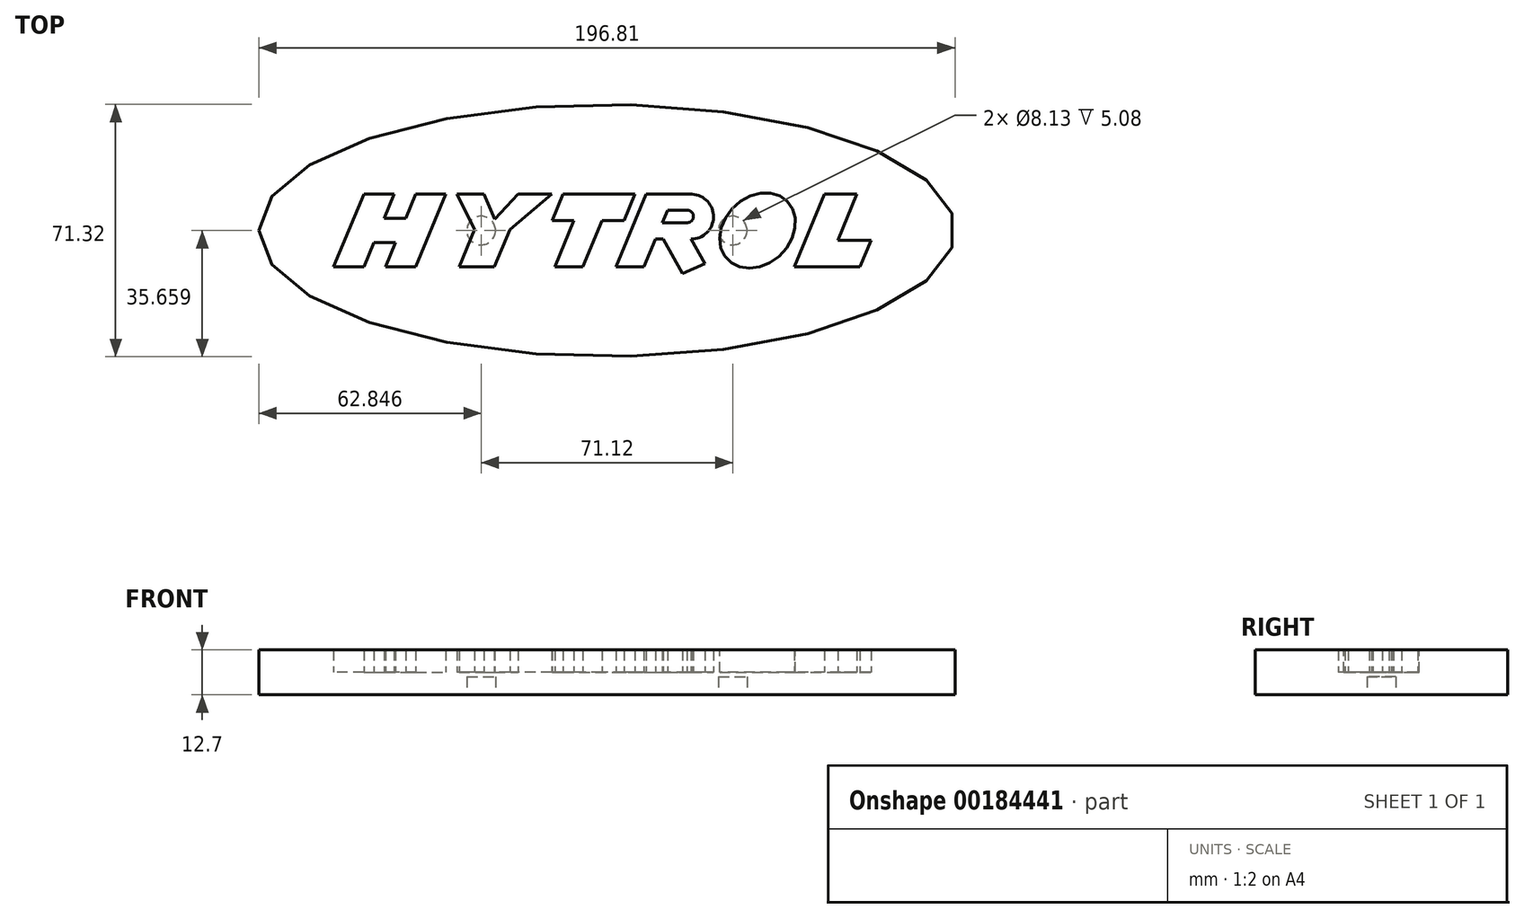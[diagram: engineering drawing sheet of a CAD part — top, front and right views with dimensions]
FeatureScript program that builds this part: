
annotation { "Feature Type Name" : "Feature", "Feature Type Description" : "" }
export const myFeature = defineFeature(function(context is Context, id is Id, definition is map)
    precondition{}
    {
        {
            var Q0;
            Q0=qCreatedBy(makeId("Top.planeOp"),FACE);
            var sketch = newSketch(context, id + "F0", { "sketchPlane" : qUnion([Q0])});
            skLineSegment(sketch, "E0", {"start": v(-38.3, -9.11) * mm, "end": v(-29.76, -9.11) * mm});
            skLineSegment(sketch, "E1", {"start": v(-29.76, 11.4) * mm, "end": v(-38.3, -9.11) * mm});
            skLineSegment(sketch, "E2", {"start": v(-29.76, 11.4) * mm, "end": v(-21.22, 11.4) * mm});
            skLineSegment(sketch, "E3", {"start": v(-6.55, 11.4) * mm, "end": v(-15.1, -9.11) * mm});
            skLineSegment(sketch, "E4", {"start": v(-15.1, -9.11) * mm, "end": v(-23.63, -9.11) * mm});
            skLineSegment(sketch, "E5", {"start": v(-23.63, -9.11) * mm, "end": v(-20.79, -2.28) * mm});
            skLineSegment(sketch, "E6", {"start": v(-29.76, -9.11) * mm, "end": v(-26.92, -2.28) * mm});
            skLineSegment(sketch, "E7", {"start": v(-26.92, -2.28) * mm, "end": v(-20.79, -2.28) * mm});
            skLineSegment(sketch, "E8", {"start": v(-21.22, 11.4) * mm, "end": v(-24.06, 4.58) * mm});
            skLineSegment(sketch, "E9", {"start": v(-24.06, 4.58) * mm, "end": v(-17.93, 4.58) * mm});
            skLineSegment(sketch, "E10.trimOffspring", {"start": v(-24.06, 4.58) * mm, "end": v(-21.22, 11.4) * mm});
            skLineSegment(sketch, "E11.trimOffspring", {"start": v(-17.93, 4.58) * mm, "end": v(-15.1, 11.4) * mm});
            skLineSegment(sketch, "E12.trimOffspring", {"start": v(-15.1, 11.4) * mm, "end": v(-6.55, 11.4) * mm});
            skLineSegment(sketch, "E13", {"start": v(-6.55, 11.4) * mm, "end": v(-3.38, 11.4) * mm, "construction": true});
            skLineSegment(sketch, "E14", {"start": v(-15.1, -9.11) * mm, "end": v(-2.83, -9.11) * mm, "construction": true});
            skLineSegment(sketch, "E15", {"start": v(-2.83, -9.11) * mm, "end": v(1.56, 1.44) * mm});
            skLineSegment(sketch, "E16", {"start": v(1.56, 1.44) * mm, "end": v(-3.38, 11.4) * mm});
            skLineSegment(sketch, "E17", {"start": v(-2.83, -9.11) * mm, "end": v(7.13, -9.11) * mm});
            skLineSegment(sketch, "E18", {"start": v(23.36, 11.4) * mm, "end": v(13.84, 11.4) * mm});
            skLineSegment(sketch, "E19", {"start": v(4.24, 11.4) * mm, "end": v(-3.38, 11.4) * mm});
            skLineSegment(sketch, "E20", {"start": v(23.36, 11.4) * mm, "end": v(11.52, 1.44) * mm});
            skLineSegment(sketch, "E21", {"start": v(11.52, 1.44) * mm, "end": v(7.13, -9.11) * mm});
            skLineSegment(sketch, "E22", {"start": v(7.17, 4.38) * mm, "end": v(13.84, 11.4) * mm});
            skLineSegment(sketch, "E23", {"start": v(2.15, -9.11) * mm, "end": v(7.17, 4.38) * mm, "construction": true});
            skLineSegment(sketch, "E24", {"start": v(4.24, 11.4) * mm, "end": v(7.17, 4.38) * mm});
            skLineSegment(sketch, "E25", {"start": v(7.13, -9.11) * mm, "end": v(24.2, -9.11) * mm, "construction": true});
            skLineSegment(sketch, "E26", {"start": v(23.36, 11.4) * mm, "end": v(26.54, 11.4) * mm, "construction": true});
            skLineSegment(sketch, "E27", {"start": v(4.24, 11.4) * mm, "end": v(13.84, 11.4) * mm, "construction": true});
            skLineSegment(sketch, "E28", {"start": v(26.54, 11.4) * mm, "end": v(23.46, 4) * mm});
            skLineSegment(sketch, "E29", {"start": v(23.46, 4) * mm, "end": v(29.66, 4) * mm});
            skLineSegment(sketch, "E30", {"start": v(29.66, 4) * mm, "end": v(24.2, -9.11) * mm});
            skLineSegment(sketch, "E31", {"start": v(26.54, 11.4) * mm, "end": v(46.88, 11.4) * mm});
            skLineSegment(sketch, "E32", {"start": v(46.88, 11.4) * mm, "end": v(43.8, 4) * mm});
            skLineSegment(sketch, "E33", {"start": v(43.8, 4) * mm, "end": v(37.6, 4) * mm});
            skLineSegment(sketch, "E34", {"start": v(37.6, 4) * mm, "end": v(32.14, -9.11) * mm});
            skLineSegment(sketch, "E35", {"start": v(32.14, -9.11) * mm, "end": v(24.2, -9.11) * mm});
            skLineSegment(sketch, "E36", {"start": v(46.88, 11.4) * mm, "end": v(50.05, 11.4) * mm, "construction": true});
            skLineSegment(sketch, "E37", {"start": v(32.14, -9.11) * mm, "end": v(41.52, -9.11) * mm, "construction": true});
            skLineSegment(sketch, "E38", {"start": v(50.05, 11.4) * mm, "end": v(41.52, -9.11) * mm});
            skLineSegment(sketch, "E39", {"start": v(41.52, -9.11) * mm, "end": v(49.45, -9.11) * mm});
            skLineSegment(sketch, "E40", {"start": v(49.45, -9.11) * mm, "end": v(52.7, -1.3) * mm});
            skLineSegment(sketch, "E41", {"start": v(52.7, -1.3) * mm, "end": v(54.9, -1.3) * mm});
            skLineSegment(sketch, "E42", {"start": v(54.9, -1.3) * mm, "end": v(60.38, -10.98) * mm});
            skLineSegment(sketch, "E43", {"start": v(50.05, 11.4) * mm, "end": v(63.03, 11.4) * mm});
            skLineSegment(sketch, "E44", {"start": v(49.45, -9.11) * mm, "end": v(71.62, -9.11) * mm, "construction": true});
            skLineSegment(sketch, "E45", {"start": v(63.03, 11.4) * mm, "end": v(86.54, 11.4) * mm, "construction": true});
            skLineSegment(sketch, "E46", {"start": v(86.54, 11.4) * mm, "end": v(100.5, 11.4) * mm, "construction": true});
            skLineSegment(sketch, "E47", {"start": v(71.62, -9.11) * mm, "end": v(91.97, -9.11) * mm, "construction": true});
            skLineSegment(sketch, "E48", {"start": v(100.5, 11.4) * mm, "end": v(91.97, -9.11) * mm});
            skLineSegment(sketch, "E49", {"start": v(91.97, -9.11) * mm, "end": v(110.51, -9.11) * mm});
            skLineSegment(sketch, "E50", {"start": v(110.51, -9.11) * mm, "end": v(113.6, -1.68) * mm});
            skLineSegment(sketch, "E51", {"start": v(113.6, -1.68) * mm, "end": v(104.2, -1.68) * mm});
            skLineSegment(sketch, "E52", {"start": v(104.2, -1.68) * mm, "end": v(109.65, 11.4) * mm});
            skLineSegment(sketch, "E53", {"start": v(109.65, 11.4) * mm, "end": v(100.5, 11.4) * mm});
            skLineSegment(sketch, "E54.2", {"start": v(56.1, 6.89) * mm, "end": v(61.64, 6.89) * mm});
            skLineSegment(sketch, "E55", {"start": v(61.67, 3.37) * mm, "end": v(54.65, 3.37) * mm});
            skArc(sketch, "E56", {"start": v(61.67, 3.37) * mm, "mid": v(63.43, 5.14) * mm, "end": v(61.64, 6.89) * mm});
            skLineSegment(sketch, "E57", {"start": v(54.65, 3.37) * mm, "end": v(56.1, 6.89) * mm});
            skLineSegment(sketch, "E58", {"start": v(62.74, -1.3) * mm, "end": v(66.64, -8.21) * mm});
            skLineSegment(sketch, "E59", {"start": v(66.64, -8.21) * mm, "end": v(60.38, -10.98) * mm});
            skEllipse(sketch, "E60", {"center": v(38.98, 1.15) * mm, "majorRadius": 35.66 * mm, "minorRadius": 98.4 * mm, "majorAxis": v(0, 1)});
            skLineSegment(sketch, "E61.trimOffspring", {"start": v(38.98, 11.4) * mm, "end": v(38.98, 36.8) * mm});
            skLineSegment(sketch, "E62", {"start": v(-34.03, 1.15) * mm, "end": v(-59.43, 1.15) * mm});
            skLineSegment(sketch, "E63", {"start": v(54.9, -1.3) * mm, "end": v(62.74, -1.3) * mm});
            skArc(sketch, "E64", {"start": v(62.74, -1.3) * mm, "mid": v(69.1, 4.91) * mm, "end": v(63.03, 11.4) * mm});
            skEllipse(sketch, "E65", {"center": v(81.53, 1.15) * mm, "majorRadius": 11.78 * mm, "minorRadius": 9.47 * mm, "majorAxis": v(0.71, 0.7)});
            skFitSpline(sketch, "E66.0", {"points": [v(86.27, 5.12) * mm, v(85.96, 5.51) * mm, v(85.57, 5.82) * mm, v(85.03, 6.08) * mm, v(84.3, 6.24) * mm, v(83.35, 6.25) * mm, v(82.25, 6.04) * mm, v(81.06, 5.58) * mm, v(79.88, 4.87) * mm, v(78.78, 3.95) * mm, v(77.83, 2.86) * mm, v(77.11, 1.7) * mm, v(76.63, 0.5) * mm, v(76.4, -0.59) * mm, v(76.4, -1.53) * mm, v(76.55, -2.27) * mm, v(76.8, -2.81) * mm, v(77.1, -3.2) * mm, v(77.49, -3.52) * mm, v(78.02, -3.77) * mm, v(78.76, -3.94) * mm, v(79.7, -3.94) * mm, v(80.8, -3.73) * mm, v(82, -3.27) * mm, v(83.18, -2.57) * mm, v(84.28, -1.65) * mm, v(85.22, -0.56) * mm, v(85.94, 0.61) * mm, v(86.42, 1.8) * mm, v(86.65, 2.9) * mm, v(86.66, 3.84) * mm, v(86.51, 4.58) * mm, v(86.27, 5.12) * mm, v(85.96, 5.51) * mm, v(85.57, 5.82) * mm, v(86.27, 5.12) * mm]});
            skLineSegment(sketch, "E67", {"start": v(1.56, 1.44) * mm, "end": v(11.52, 1.44) * mm, "construction": true});
            skSolve(sketch);
        }
        {
            var Q0;
            {var subQ20=sQuery(id+"F0.wireOp",EDGE,"E2");Q0=makeQuery(id+"F0.imprint","IMPRINT",FACE,{"disambiguationData":[TD([[makeQuery(id+"F0.imprint","IMPRINT",EDGE,{"derivedFrom":subQ20}),1.0]])]});}
            var Q1;
            {var subQ20=sQuery(id+"F0.wireOp",EDGE,"E0");Q1=makeQuery(id+"F0.imprint","IMPRINT",FACE,{"disambiguationData":[TD([[makeQuery(id+"F0.imprint","IMPRINT",EDGE,{"derivedFrom":subQ20}),-1.0]])]});}
            var Q2;
            {var subQ0=sQuery(id+"F0.wireOp",EDGE,"E34");var subQ1=sQuery(id+"F0.wireOp",EDGE,"E33");var subQ2=makeQuery(id+"F0.imprint","INTERSECT",VERTEX,{"derivedFrom":[subQ1,subQ0]});Q2=makeQuery(id+"F0.imprint","IMPRINT",FACE,{"disambiguationData":[TD([[makeQuery(id+"F0.imprint","IMPRINT",EDGE,{"disambiguationData":[TD([[subQ2,1.0]])],"derivedFrom":subQ1}),1.0]])]});}
            var Q3;
            Q3=makeQuery(id+"F0.imprint","IMPRINT",FACE,{"disambiguationData":[TD([[makeQuery(id+"F0.imprint","IMPRINT",EDGE,{"derivedFrom":sQuery(id+"F0.wireOp",EDGE,"jYYLCyd6-I7t1-1UZf-D7tA-eIDzwACRAnDD")}),1.0]])]});
            extrude(context, id + "F1", {"entities" : qUnion([Q0, Q1, Q2, Q3]), "depth" : 12.7 * mm});
        }
        {
            var Q0;
            {var subQ0=sQuery(id+"F0.wireOp",EDGE,"E2");Q0=makeQuery(id+"F0.imprint","IMPRINT",FACE,{"disambiguationData":[TD([[makeQuery(id+"F0.imprint","IMPRINT",EDGE,{"derivedFrom":subQ0}),-1.0]])]});}
            var Q1;
            {var subQ5=sQuery(id+"F0.wireOp",EDGE,"E0");Q1=makeQuery(id+"F0.imprint","IMPRINT",FACE,{"disambiguationData":[TD([[makeQuery(id+"F0.imprint","IMPRINT",EDGE,{"derivedFrom":subQ5}),1.0]])]});}
            var Q2;
            {var subQ0=sQuery(id+"F0.wireOp",EDGE,"E17");Q2=makeQuery(id+"F0.imprint","IMPRINT",FACE,{"disambiguationData":[TD([[makeQuery(id+"F0.imprint","IMPRINT",EDGE,{"derivedFrom":subQ0}),1.0]])]});}
            var Q3;
            {var subQ0=sQuery(id+"F0.wireOp",EDGE,"E16");Q3=makeQuery(id+"F0.imprint","IMPRINT",FACE,{"disambiguationData":[TD([[makeQuery(id+"F0.imprint","IMPRINT",EDGE,{"derivedFrom":subQ0}),-1.0]])]});}
            var Q4;
            {var subQ1=sQuery(id+"F0.wireOp",EDGE,"E28");Q4=makeQuery(id+"F0.imprint","IMPRINT",FACE,{"disambiguationData":[TD([[makeQuery(id+"F0.imprint","IMPRINT",EDGE,{"derivedFrom":subQ1}),1.0]])]});}
            var Q5;
            {var subQ0=sQuery(id+"F0.wireOp",EDGE,"E35");Q5=makeQuery(id+"F0.imprint","IMPRINT",FACE,{"disambiguationData":[TD([[makeQuery(id+"F0.imprint","IMPRINT",EDGE,{"derivedFrom":subQ0}),-1.0]])]});}
            var Q6;
            {var subQ0=sQuery(id+"F0.wireOp",EDGE,"E32");Q6=makeQuery(id+"F0.imprint","IMPRINT",FACE,{"disambiguationData":[TD([[makeQuery(id+"F0.imprint","IMPRINT",EDGE,{"derivedFrom":subQ0}),-1.0]])]});}
            var Q7;
            Q7=makeQuery(id+"F0.imprint","IMPRINT",FACE,{"disambiguationData":[TD([[makeQuery(id+"F0.imprint","IMPRINT",EDGE,{"derivedFrom":sQuery(id+"F0.wireOp",EDGE,"E38")}),1.0]])]});
            var Q8;
            Q8=makeQuery(id+"F0.imprint","IMPRINT",FACE,{"disambiguationData":[TD([[makeQuery(id+"F0.imprint","IMPRINT",EDGE,{"derivedFrom":sQuery(id+"F0.wireOp",EDGE,"BcMKju4M-TPsr-44tH-nnLG-ZhNeSZutTXem")}),1.0]])]});
            var Q9;
            Q9=makeQuery(id+"F0.imprint","IMPRINT",FACE,{"disambiguationData":[TD([[makeQuery(id+"F0.imprint","IMPRINT",EDGE,{"derivedFrom":sQuery(id+"F0.wireOp",EDGE,"E42")}),1.0]])]});
            var Q10;
            Q10=makeQuery(id+"F0.imprint","IMPRINT",FACE,{"disambiguationData":[TD([[makeQuery(id+"F0.imprint","IMPRINT",EDGE,{"derivedFrom":sQuery(id+"F0.wireOp",EDGE,"5b522tZx-uF20-0fNL-tGMi-Xu5gsHFENX20")}),1.0]])]});
            var Q11;
            Q11=makeQuery(id+"F0.imprint","IMPRINT",FACE,{"disambiguationData":[TD([[makeQuery(id+"F0.imprint","IMPRINT",EDGE,{"derivedFrom":sQuery(id+"F0.wireOp",EDGE,"E48")}),1.0]])]});
            var Q12;
            Q12=makeQuery(id+"F0.imprint","IMPRINT",FACE,{"disambiguationData":[TD([[makeQuery(id+"F0.imprint","IMPRINT",EDGE,{"derivedFrom":sQuery(id+"F0.wireOp",EDGE,"E65")}),1.0]])]});
            extrude(context, id + "F2", {"entities" : qUnion([Q0, Q1, Q2, Q3, Q4, Q5, Q6, Q7, Q8, Q9, Q10, Q11, Q12]), "operationType" : NewBodyOperationType.ADD, "depth" : 6.35 * mm});
        }
        {
            var Q0;
            {var subQ0=sQuery(id+"F0.wireOp",EDGE,"E66.0");var subQ1=sQuery(id+"F0.wireOp",EDGE,"E57");var subQ2=sQuery(id+"F0.wireOp",EDGE,"E56");var subQ3=sQuery(id+"F0.wireOp",EDGE,"E55");var subQ4=sQuery(id+"F0.wireOp",EDGE,"E54.2");var subQ5=sQuery(id+"F0.wireOp",EDGE,"E65");var subQ6=sQuery(id+"F0.wireOp",EDGE,"E53");var subQ7=sQuery(id+"F0.wireOp",EDGE,"E52");var subQ8=sQuery(id+"F0.wireOp",EDGE,"E51");var subQ9=sQuery(id+"F0.wireOp",EDGE,"E50");var subQ10=sQuery(id+"F0.wireOp",EDGE,"E49");var subQ11=sQuery(id+"F0.wireOp",EDGE,"E48");var subQ12=sQuery(id+"F0.wireOp",EDGE,"E64");var subQ13=sQuery(id+"F0.wireOp",EDGE,"E59");var subQ14=sQuery(id+"F0.wireOp",EDGE,"E58");var subQ15=sQuery(id+"F0.wireOp",EDGE,"E43");var subQ16=sQuery(id+"F0.wireOp",EDGE,"E42");var subQ17=sQuery(id+"F0.wireOp",EDGE,"E41");var subQ18=sQuery(id+"F0.wireOp",EDGE,"E40");var subQ19=sQuery(id+"F0.wireOp",EDGE,"E39");var subQ20=sQuery(id+"F0.wireOp",EDGE,"E38");var subQ21=sQuery(id+"F0.wireOp",EDGE,"E35");var subQ22=sQuery(id+"F0.wireOp",EDGE,"E34");var subQ23=sQuery(id+"F0.wireOp",EDGE,"E33");var subQ24=sQuery(id+"F0.wireOp",EDGE,"E32");var subQ25=sQuery(id+"F0.wireOp",EDGE,"E31");var subQ26=sQuery(id+"F0.wireOp",EDGE,"E30");var subQ27=sQuery(id+"F0.wireOp",EDGE,"E29");var subQ28=sQuery(id+"F0.wireOp",EDGE,"E28");var subQ29=sQuery(id+"F0.wireOp",EDGE,"E24");var subQ30=sQuery(id+"F0.wireOp",EDGE,"E22");var subQ31=sQuery(id+"F0.wireOp",EDGE,"E21");var subQ32=sQuery(id+"F0.wireOp",EDGE,"E20");var subQ33=sQuery(id+"F0.wireOp",EDGE,"E19");var subQ34=sQuery(id+"F0.wireOp",EDGE,"E18");var subQ35=sQuery(id+"F0.wireOp",EDGE,"E17");var subQ36=sQuery(id+"F0.wireOp",EDGE,"E16");var subQ37=sQuery(id+"F0.wireOp",EDGE,"E15");var subQ38=sQuery(id+"F0.wireOp",EDGE,"E12.trimOffspring");var subQ39=sQuery(id+"F0.wireOp",EDGE,"E11.trimOffspring");var subQ40=sQuery(id+"F0.wireOp",EDGE,"E10.trimOffspring");var subQ41=sQuery(id+"F0.wireOp",EDGE,"E9");var subQ42=sQuery(id+"F0.wireOp",EDGE,"E7");var subQ43=sQuery(id+"F0.wireOp",EDGE,"E6");var subQ44=sQuery(id+"F0.wireOp",EDGE,"E5");var subQ45=sQuery(id+"F0.wireOp",EDGE,"E4");var subQ46=sQuery(id+"F0.wireOp",EDGE,"E3");var subQ47=sQuery(id+"F0.wireOp",EDGE,"E2");var subQ48=sQuery(id+"F0.wireOp",EDGE,"E1");var subQ49=sQuery(id+"F0.wireOp",EDGE,"E0");Q0=makeQuery(id+"Fz2jGoP8NZOWLJ9_1.boolean.opBoolean","MERGE",FACE,{"derivedFrom":[makeQuery(id+"F2.boolean.opBoolean","MERGE",FACE,{"derivedFrom":[makeQuery(id+"F1.opExtrude","CAP_FACE",FACE,{"disambiguationData":[OSD([subQ49,subQ48,subQ47,subQ46,subQ45,subQ44,subQ43,subQ42,subQ41,subQ40,subQ39,subQ38,subQ37,subQ36,subQ35,subQ34,subQ33,subQ32,subQ31,subQ30,subQ29,subQ28,subQ27,subQ26,subQ25,subQ24,subQ23,subQ22,subQ21,subQ20,subQ19,subQ18,subQ17,subQ16,subQ15,subQ11,subQ10,subQ9,subQ8,subQ7,subQ6,subQ14,subQ13,sQuery(id+"F0.wireOp",EDGE,"E60"),subQ12,subQ5])],"isStart":true}),makeQuery(id+"F2.opExtrude","CAP_FACE",FACE,{"disambiguationData":[OSD([subQ49,subQ48,subQ47,subQ46,subQ45,subQ44,subQ43,subQ42,subQ41,subQ40,subQ39,subQ38])],"isStart":true}),makeQuery(id+"F2.opExtrude","CAP_FACE",FACE,{"disambiguationData":[OSD([subQ37,subQ36,subQ35,subQ34,subQ33,subQ32,subQ31,subQ30,subQ29])],"isStart":true}),makeQuery(id+"F2.opExtrude","CAP_FACE",FACE,{"disambiguationData":[OSD([subQ28,subQ27,subQ26,subQ25,subQ24,subQ23,subQ22,subQ21])],"isStart":true}),makeQuery(id+"F2.opExtrude","CAP_FACE",FACE,{"disambiguationData":[OSD([subQ20,subQ19,subQ18,subQ17,subQ16,subQ15,subQ4,subQ3,subQ2,subQ1,subQ14,subQ13,subQ12])],"isStart":true}),makeQuery(id+"F2.opExtrude","CAP_FACE",FACE,{"disambiguationData":[OSD([subQ11,subQ10,subQ9,subQ8,subQ7,subQ6])],"isStart":true}),makeQuery(id+"F2.opExtrude","CAP_FACE",FACE,{"disambiguationData":[OSD([subQ5,subQ0])],"isStart":true})]}),makeQuery(id+"Fz2jGoP8NZOWLJ9_1.opExtrude","CAP_FACE",FACE,{"disambiguationData":[OSD([subQ4,subQ3,subQ2,subQ1])],"isStart":true}),makeQuery(id+"Fz2jGoP8NZOWLJ9_1.opExtrude","CAP_FACE",FACE,{"disambiguationData":[OSD([subQ0])],"isStart":true})]});}
            var sketch = newSketch(context, id + "F3", { "sketchPlane" : qUnion([Q0])});
            skPoint(sketch, "E68.orphan", {"position": v(137.38, -1.15) * mm});
            skLineSegment(sketch, "E69", {"start": v(38.98, -1.15) * mm, "end": v(74.54, -1.15) * mm});
            skPoint(sketch, "E70.start.orphan", {"position": v(-59.43, -1.15) * mm});
            skLineSegment(sketch, "E71", {"start": v(38.98, -1.15) * mm, "end": v(3.42, -1.15) * mm});
            skCircle(sketch, "E72", {"center": v(74.54, -1.15) * mm, "radius": 4.06 * mm});
            skCircle(sketch, "E73", {"center": v(3.42, -1.15) * mm, "radius": 4.06 * mm});
            skLineSegment(sketch, "E74", {"start": v(38.98, -1.15) * mm, "end": v(38.98, 34.51) * mm});
            skLineSegment(sketch, "E75", {"start": v(38.98, -1.15) * mm, "end": v(38.98, -36.8) * mm});
            skSolve(sketch);
        }
        {
            var Q0;
            Q0=makeQuery(id+"F3.imprint","IMPRINT",FACE,{"disambiguationData":[TD([[makeQuery(id+"F3.imprint","IMPRINT",EDGE,{"derivedFrom":sQuery(id+"F3.wireOp",EDGE,"E73")}),1.0]])]});
            var Q1;
            Q1=makeQuery(id+"F3.imprint","IMPRINT",FACE,{"disambiguationData":[TD([[makeQuery(id+"F3.imprint","IMPRINT",EDGE,{"derivedFrom":sQuery(id+"F3.wireOp",EDGE,"E72")}),1.0]])]});
            extrude(context, id + "F4", {"entities" : qUnion([Q0, Q1]), "operationType" : NewBodyOperationType.REMOVE, "oppositeDirection" : true, "depth" : 5.08 * mm});
        }
        {
            var Q0;
            Q0=makeQuery(id+"F0.imprint","IMPRINT",FACE,{"disambiguationData":[TD([[makeQuery(id+"F0.imprint","IMPRINT",EDGE,{"derivedFrom":sQuery(id+"F0.wireOp",EDGE,"E54.2")}),-1.0]])]});
            var Q1;
            Q1=makeQuery(id+"F0.imprint","IMPRINT",FACE,{"disambiguationData":[TD([[makeQuery(id+"F0.imprint","IMPRINT",EDGE,{"derivedFrom":sQuery(id+"F0.wireOp",EDGE,"E66.0")}),1.0]])]});
            extrude(context, id + "F5", {"entities" : qUnion([Q0, Q1]), "operationType" : NewBodyOperationType.ADD, "depth" : 12.7 * mm});
        }
    });
